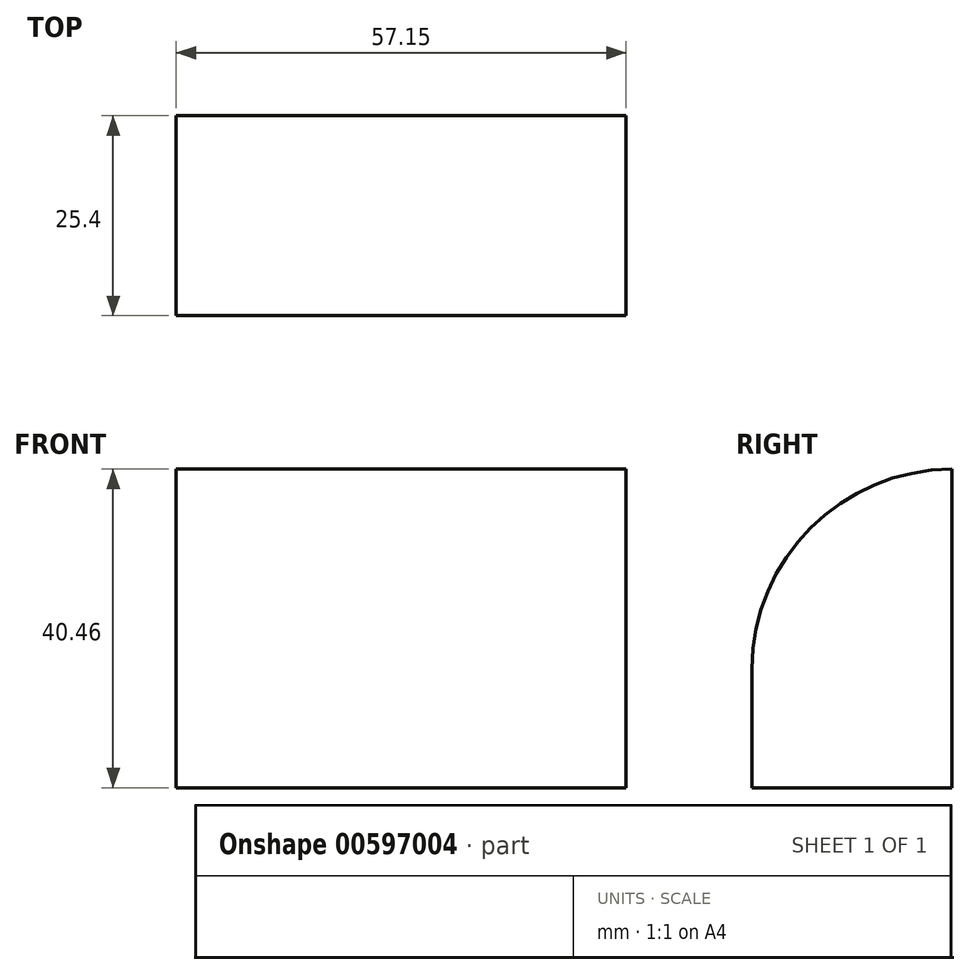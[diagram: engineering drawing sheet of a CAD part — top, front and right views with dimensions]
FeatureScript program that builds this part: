
annotation { "Feature Type Name" : "Feature", "Feature Type Description" : "" }
export const myFeature = defineFeature(function(context is Context, id is Id, definition is map)
    precondition{}
    {
        {
            var Q0;
            Q0=qCreatedBy(makeId("Front.planeOp"),FACE);
            var sketch = newSketch(context, id + "F0", { "sketchPlane" : qUnion([Q0])});
            skLineSegment(sketch, "E0", {"start": v(-57.15, 40.46) * mm, "end": v(0, 40.46) * mm});
            skLineSegment(sketch, "E1", {"start": v(0, 40.46) * mm, "end": v(0, 0) * mm});
            skLineSegment(sketch, "E2", {"start": v(0, 0) * mm, "end": v(-57.15, 0) * mm});
            skLineSegment(sketch, "E3", {"start": v(-57.15, 0) * mm, "end": v(-57.15, 40.46) * mm});
            skSolve(sketch);
        }
        {
            var Q0;
            Q0=makeQuery(id+"F0.imprint","IMPRINT",FACE,{"disambiguationData":[TD([[makeQuery(id+"F0.imprint","IMPRINT",EDGE,{"derivedFrom":sQuery(id+"F0.wireOp",EDGE,"E0")}),-1.0]])]});
            extrude(context, id + "F1", {"entities" : qUnion([Q0]), "depth" : 25.4 * mm, "offsetDistance" : 25.4 * mm});
        }
        {
            var Q0;
            Q0=makeQuery(id+"F1.opExtrude","CAP_EDGE",EDGE,{"disambiguationData":[OSD([sQuery(id+"F0.wireOp",EDGE,"E0")])],"isStart":false});
            fillet(context, id + "F2", {"entities" : qUnion([Q0]), "radius" : 25.4 * mm, "tangentPropagation" : true, "allowEdgeOverflow" : false});
        }
    });
